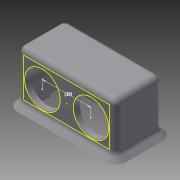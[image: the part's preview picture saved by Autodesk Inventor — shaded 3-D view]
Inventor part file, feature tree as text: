
AUTODESK INVENTOR PART (.ipt)
format: ipt  version: 2014 SP2 (Build 180246200, 246)  size: 301,056 bytes
history: native  units: mm
features: extrude x7, sketch x7, fillet x5, chamfer x2
ambient origin geometry x8: Origin, YZ Plane, XZ Plane, XY Plane, X Axis, Y Axis, Z Axis, Center Point
bodies: Solid1 (feature_tree)
feature tree (21):
  extrude  "Extrusion1"  Depth=28.0mm
  extrude  "Extrusion2"  Depth=14.0mm
  extrude  "Extrusion3"  Depth=3.0mm
  extrude  "Extrusion4"  Depth=13.0mm
  fillet  "Fillet1"  Radius=13.0mm
  extrude  "Extrusion5"  Depth=52.0mm
  fillet  "Fillet4"  Radius=14.0mm
  chamfer  "Chamfer1"  Distance=13.0mm
  fillet  "Fillet5"  Radius=3.0mm
  extrude  "Extrusion6"  Depth=46.0mm
  fillet  "Fillet7"  Radius=22.0mm
  chamfer  "Chamfer3"  Distance=17.0mm
  fillet  "Fillet8"  Radius=1.5mm
  extrude  "Extrusion8"  Depth=25.0mm
  sketch  "Sketch1"  dims[d0=52.0mm d1=28.0mm]
  sketch  "Sketch2"  dims[d2=26.0mm d3=14.0mm]
  sketch  "Sketch3"  dims[d4=3.0mm d5=0.0mm d6=18.0mm]
  sketch  "Sketch4"  dims[d7=18.0mm d8=26.0mm d9=13.0mm]
  sketch  "Sketch5"  dims[d10=8.0mm d11=0.0mm d12=52.0mm d14=14.0mm]
  sketch  "Sketch6"  dims[d15=28.0mm]
  sketch  "Sketch8"  dims[d17=14.0mm d18=13.0mm d19=3.0mm d20=46.0mm d21=22.0mm d22=17.0mm d23=0.0mm d27=1.5mm d28=25.0mm d29=0.0mm d31=1.5mm d32=25.0mm d33=0.0mm d34=8.5mm d35=10.0mm d36=0.0mm d37=0.0mm d38=18.0mm d39=2.0mm d42=5.0mm d43=0.0mm d44=2.0mm d45=23.0mm d46=2.0mm d47=45.0deg d48=3.0mm d49=3.0mm d50=3.0mm d51=0.0mm d60=0.5mm d61=3.0mm d62=2.0mm d63=45.0deg d64=3.0mm d65=1.5mm d66=1.0mm d67=1.0mm d68=0.0mm]
